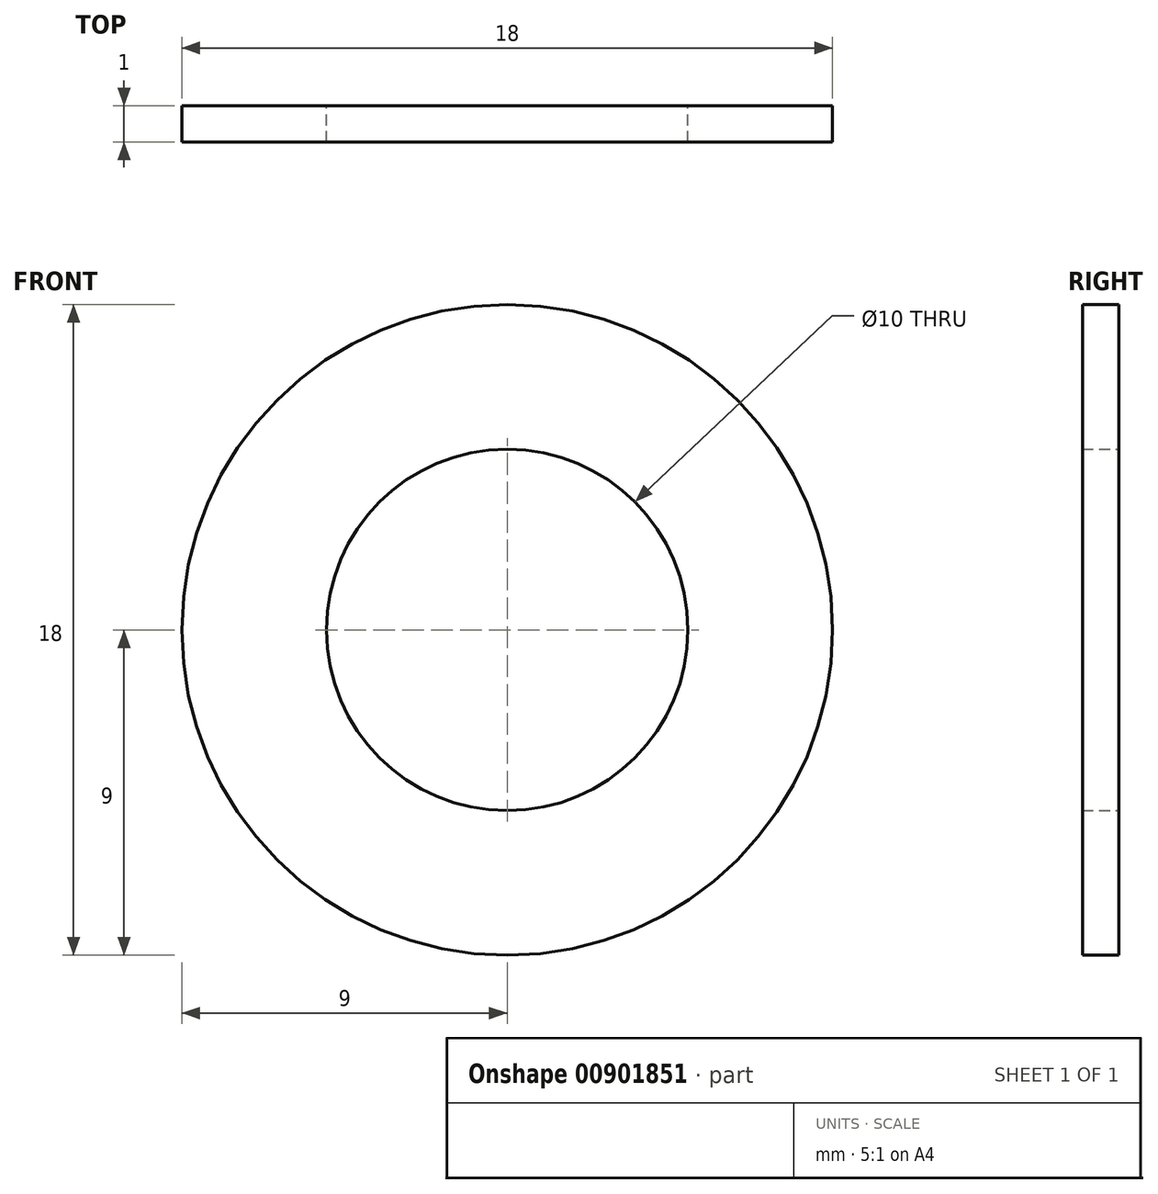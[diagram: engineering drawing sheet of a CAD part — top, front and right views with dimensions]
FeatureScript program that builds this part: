
annotation { "Feature Type Name" : "Feature", "Feature Type Description" : "" }
export const myFeature = defineFeature(function(context is Context, id is Id, definition is map)
    precondition{}
    {
        {
            var Q0;
            Q0=qCreatedBy(makeId("Front.planeOp"),FACE);
            var sketch = newSketch(context, id + "F0", { "sketchPlane" : qUnion([Q0])});
            skCircle(sketch, "E0", {"center": v(0, 0) * mm, "radius": 9 * mm});
            skCircle(sketch, "E1", {"center": v(0, 0) * mm, "radius": 5 * mm});
            skSolve(sketch);
        }
        {
            var Q0;
            Q0 = qSketchRegion(id + "F0", true);
            extrude(context, id + "F1", {"entities" : qUnion([Q0]), "depth" : 1 * mm, "offsetDistance" : 25 * mm});
        }
    });
